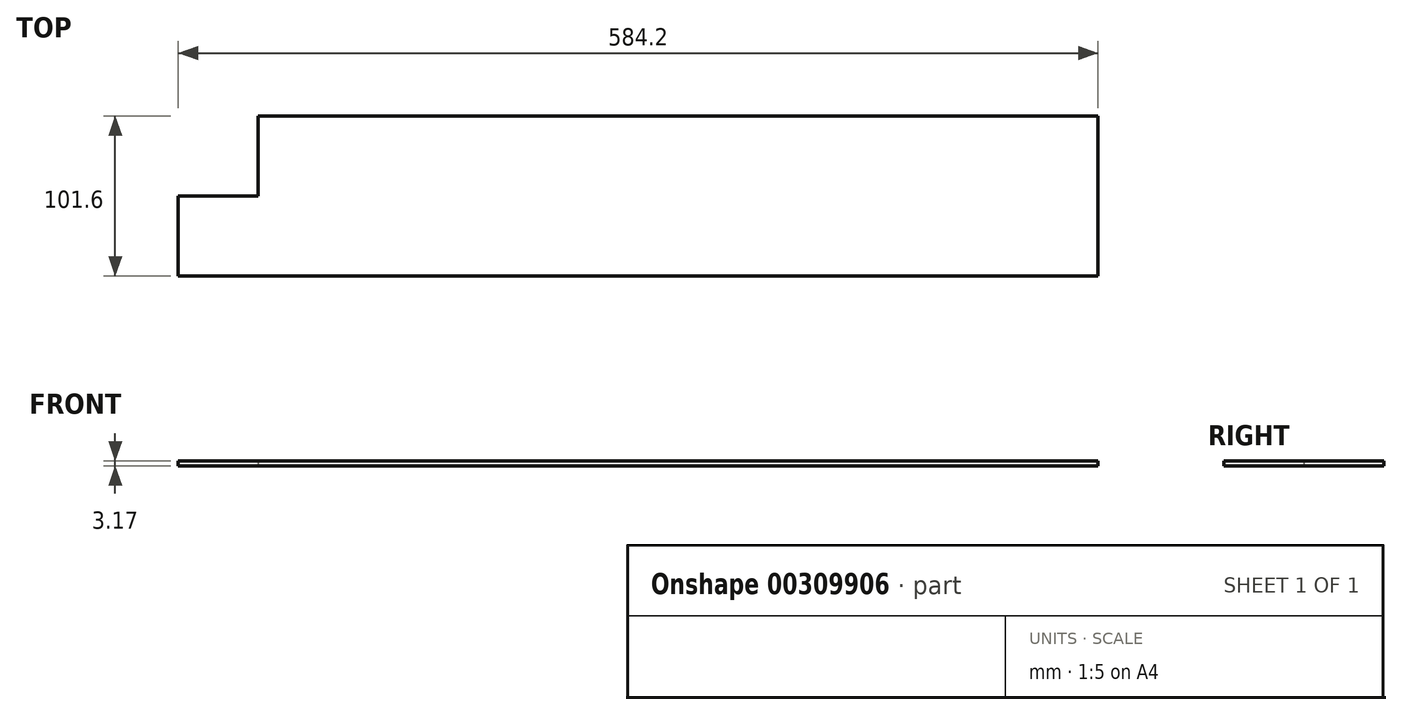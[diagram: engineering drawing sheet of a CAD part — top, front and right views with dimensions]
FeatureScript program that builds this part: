
annotation { "Feature Type Name" : "Feature", "Feature Type Description" : "" }
export const myFeature = defineFeature(function(context is Context, id is Id, definition is map)
    precondition{}
    {
        {
            var Q0;
            Q0=qCreatedBy(makeId("Top.planeOp"),FACE);
            var sketch = newSketch(context, id + "F0", { "sketchPlane" : qUnion([Q0])});
            skLineSegment(sketch, "E0.bottom", {"start": v(0, 0) * mm, "end": v(584.2, 0) * mm});
            skLineSegment(sketch, "E0.top", {"start": v(50.8, 101.6) * mm, "end": v(584.2, 101.6) * mm});
            skLineSegment(sketch, "E0.left", {"start": v(0, 0) * mm, "end": v(0, 50.8) * mm});
            skLineSegment(sketch, "E0.right", {"start": v(584.2, 0) * mm, "end": v(584.2, 101.6) * mm});
            skLineSegment(sketch, "E1", {"start": v(50.8, 50.8) * mm, "end": v(0, 50.8) * mm});
            skLineSegment(sketch, "E2", {"start": v(50.8, 50.8) * mm, "end": v(50.8, 101.6) * mm});
            skSolve(sketch);
        }
        {
            var Q0;
            Q0=makeQuery(id+"F0.imprint","IMPRINT",FACE,{"disambiguationData":[TD([[makeQuery(id+"F0.imprint","IMPRINT",EDGE,{"derivedFrom":sQuery(id+"F0.wireOp",EDGE,"E0.bottom")}),1.0]])]});
            extrude(context, id + "F1", {"entities" : qUnion([Q0]), "depth" : 3.17 * mm});
        }
    });
